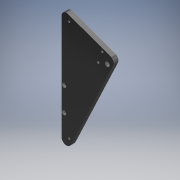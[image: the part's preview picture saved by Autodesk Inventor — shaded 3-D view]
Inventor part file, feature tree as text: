
AUTODESK INVENTOR PART (.ipt)
format: ipt  version: 2019 (Build 230136000, 136)  size: 151,552 bytes
history: native  units: mm (DEFAULTED — no unit token found)
features: sketch x6, extrude x5, fillet x2, hole x1
ambient origin geometry x8: Origin, YZ Plane, XZ Plane, XY Plane, X Axis, Y Axis, Z Axis, Center Point
bodies: Solid1 (feature_tree)
feature tree (14):
  extrude  "Extrusion1"  Depth=6.35mm TaperAngle=0.0deg
  fillet  "Fillet1"  Radius=6.35mm
  fillet  "Fillet4"  Radius=76.2mm
  extrude  "Extrusion3"  Depth=6.35mm
  extrude  "Extrusion4"  Depth=3.048mm
  extrude  "Extrusion5"  Depth=3.175mm
  hole  "Hole1"  [1 undecoded]
  extrude  "Extrusion6"  Depth=3.175mm
  sketch  "Sketch1"  dims[d0=177.8mm d2=6.35mm d3=0.0mm d4=6.35mm d19=76.2mm]
  sketch  "Sketch3"  dims[d20=3.490659mm d21=6.35mm]
  sketch  "Sketch4"  dims[d22=3.048mm d23=3.048mm]
  sketch  "Sketch5"  dims[d24=3.175mm d25=3.175mm]
  sketch  "Sketch6"  dims[d26=29.845mm d27=31.75mm]
  sketch  "Sketch7"  dims[d28=25.4mm d29=0.0mm d30=5.842mm d31=5.842mm d32=3.556mm d33=0.0mm d34=6.35mm d35=52.2732mm d36=31.5976mm d37=25.4mm d38=0.0mm d39=10.0076mm d40=1.905mm d41=136.905mm d42=0.0mm d43=3.0mm d44=19.05mm d45=9.525mm d46=6.35mm d47=14.3117mm d48=25.4mm d49=20.594885mm d52=3.81mm d53=19.812mm d54=15.3162mm d55=16.8656mm d56=3.175mm d57=3.175mm d58=25.4mm d59=0.0mm]
note: 1 required parameter value undecoded (feature->parameter linkage not recoverable at this tier; creation-order binding heuristic only, values carry confidence <= 0.55)
